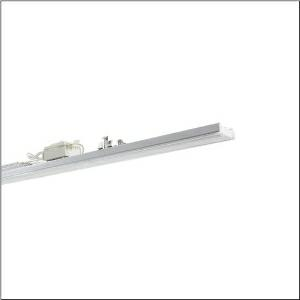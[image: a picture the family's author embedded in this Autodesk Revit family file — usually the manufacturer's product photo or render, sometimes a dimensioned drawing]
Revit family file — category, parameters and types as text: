
# Revit family: licross_21_recessed_ho_52tl11mn4fxs
name_source: partatom
category: Lighting Fixtures
units: mm (PartAtom-declared; Revit-internal decimal feet)

## family parameters
Cut with Voids When Loaded = No
Host = Face
Light Source = No
Part Type = Normal
Room Calculation Point = No
Round Connector Dimension = Use Diameter
Shared = No

## types (1)
- --- (1 x LED, 15070 lm, 83.1 W, 4000K)
    Apparent Load = 83 VA
    CIE Flux Codes = 87 95 99 100 100
    Color Rendering = 80
    Color Temperature = 4000K
    Default Elevation = 1800 mm
    Description = Licross 21 Recessed HO, luminaire insert, of sheet steel, galvanised, coil coated, white, length: 1.500mm, width: 66mm, height: 67mm, LED rated luminous flux: 15.060lm, light colour: 840, SDCM (Standard Deviation of Colour Matching)MacAdam ≤ 3 SDCM (initial), control gear: ON/OFF Multilumen, with plug, 3-pole, with phase selection, mains connection: 220..240V, AC, 50/60Hz, rated input power: 83W, internal wiring halogen-free, primary light control with lens, of plastic, primary optical cover: cover, of PMMA, light emission: direct distribution, primary light characteristic: symmetric, protection rating (complete): IP40, insulation class (complete): insulation class I (protective earthing), certification: CE, ENEC, VDE, UKCA, protection symbol: D if used in an environment without relevant dust loads with corresponding accessories, impact resistance: IK06, permissible ambient temperature for indoor applications: -35..+30°C, corresponds to IFS (International Featured Standards) requirements for safety and quality in the food industry, reducing of maximum allowable ambient temperature of 5°C with ceiling mounting, LABS conformity tested according to VDMA 24364:2018-05, The light source and the operating device comply with the requirements of the Ecodesign Regulation (EU) 2019/2020 and are replaceable in accordance with this regulation, packaging unit: 1 piece
    Height = 58 mm
    Lamp = 1 x LED
    Lamp Light Flux = 15070 lm
    Lamp Power = 83.1 W
    Lamp count = 1
    Length = 1500 mm
    Luminous efficacy = 181 lm/W
    Manufacturer = Siteco
    ModVariant = No
    Model = 52TL11MN4FXS
    Mounting Place = Ceiling
    Mounting Type = Pendant
    Number of Poles = 1
    OnlyDefault = Yes
    Power Factor = 1
    Product Name = Licross 21 Recessed HO
    Product group = luminaire insert | ceiling pendant
    ProductGroupID = 901
    Protection Class = Protection class I
    Protection Degree = IP 40
    RLX_Detail_Level = 1
    RLX_Emergency_Light_Flux = 0 lm
    RLX_Emergency_Type = 0
    RLX_Emergency_Type_DB = No
    RlxData = <blob elided: 22481 chars, md5=174ef888>
    Socket = socket
    Standby Power = 0 W
    System Light Flux = 15070 lm
    System Power = 83 W
    Type Comments = factory setting: luminous flux: 100 % | (A | C | E) | 195 mA
    Type Image = l_1296930.jpg
    URL = http://relux.com
    VarID = @adj_108011
    Voltage = 0 V
    Weight = 0.00 kg
    Width = 66 mm

## geometry (parser evidence)
native form markers: Blend x4, Sweep x10
no freeform markers — native parametric forms only
